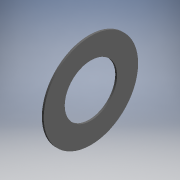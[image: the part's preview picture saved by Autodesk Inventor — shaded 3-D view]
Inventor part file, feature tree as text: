
AUTODESK INVENTOR PART (.ipt)
format: ipt  version: 2017.3 (Build 213256000, 256)  size: 95,232 bytes
history: native  units: mm (DEFAULTED — no unit token found)
features: other x7, revolve x1, sketch x1
ambient origin geometry x8: Origin, YZ Plane, XZ Plane, XY Plane, X Axis, Y Axis, Z Axis, Center Point
bodies: Solid1 (feature_tree)
feature tree (9):
  revolve  "Revolution1"  [1 undecoded]
  other  "ip_st_1_XY"
  other  "ip_st_1_YZ"
  other  "ip_st_1_ZX"
  other  "ip_st_1_X"
  other  "ip_st_1_Y"
  other  "ip_st_1_Z"
  other  "ip_st_1_Center"
  sketch  "Sketch_1"  dims[d0=360.0deg d1=0.0mm]
note: 1 required parameter value undecoded (feature->parameter linkage not recoverable at this tier; creation-order binding heuristic only, values carry confidence <= 0.55)
